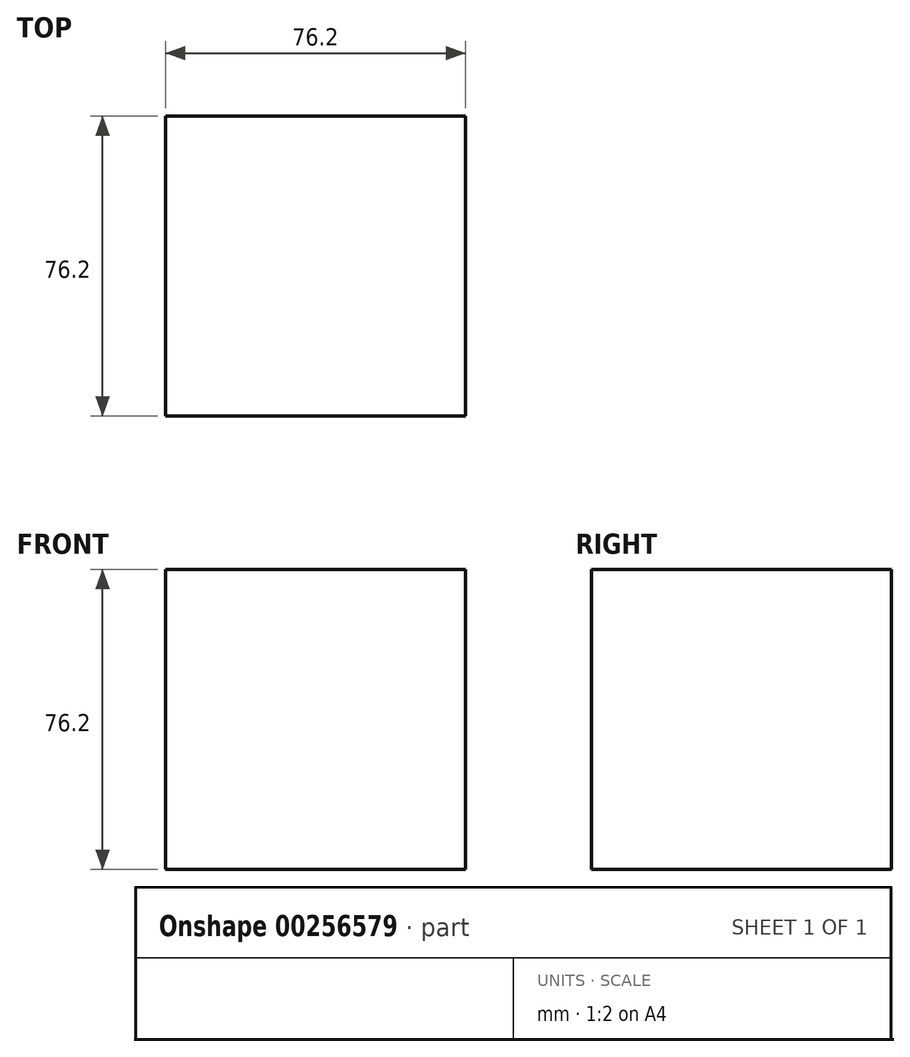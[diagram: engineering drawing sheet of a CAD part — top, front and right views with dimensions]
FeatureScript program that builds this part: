
annotation { "Feature Type Name" : "Feature", "Feature Type Description" : "" }
export const myFeature = defineFeature(function(context is Context, id is Id, definition is map)
    precondition{}
    {
        {
            var Q0;
            Q0=qCreatedBy(makeId("Front.planeOp"),FACE);
            var sketch = newSketch(context, id + "F0", { "sketchPlane" : qUnion([Q0])});
            skLineSegment(sketch, "E0.bottom", {"start": v(-38.1, -38.1) * mm, "end": v(38.1, -38.1) * mm});
            skLineSegment(sketch, "E0.top", {"start": v(-38.1, 38.1) * mm, "end": v(38.1, 38.1) * mm});
            skLineSegment(sketch, "E0.left", {"start": v(-38.1, -38.1) * mm, "end": v(-38.1, 38.1) * mm});
            skLineSegment(sketch, "E0.right", {"start": v(38.1, -38.1) * mm, "end": v(38.1, 38.1) * mm});
            skPoint(sketch, "E0.middle", {"position": v(0, 0) * mm});
            skSolve(sketch);
        }
        {
            var Q0;
            Q0 = qSketchRegion(id + "F0", true);
            extrude(context, id + "F1", {"entities" : qUnion([Q0]), "depth" : 76.2 * mm});
        }
    });
